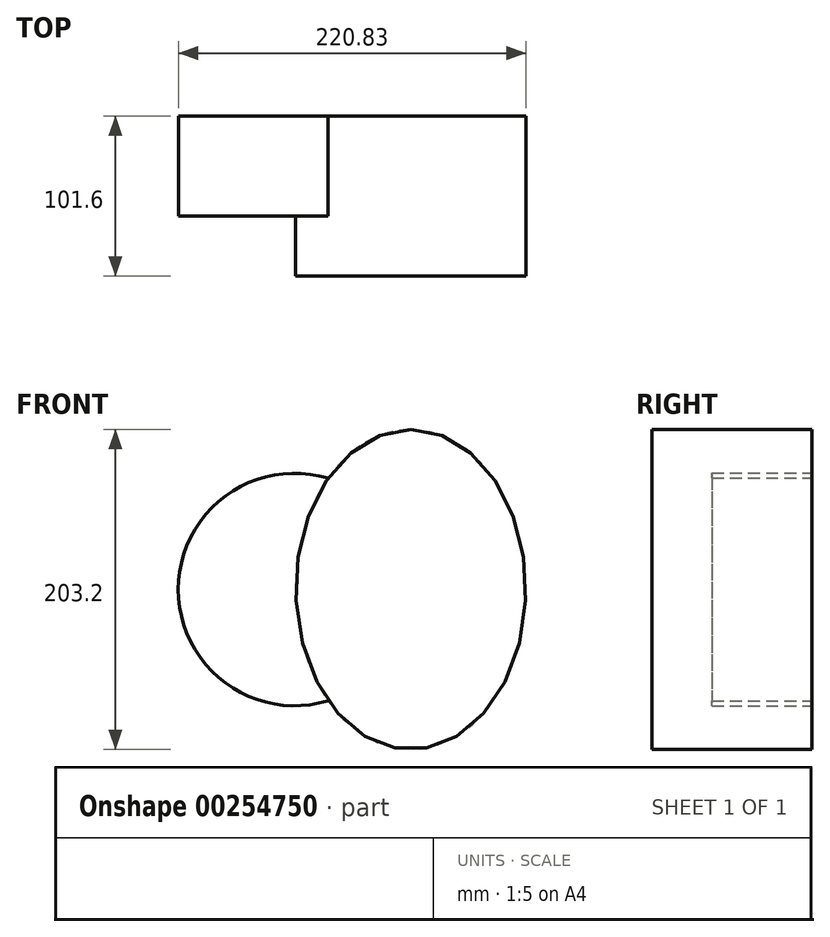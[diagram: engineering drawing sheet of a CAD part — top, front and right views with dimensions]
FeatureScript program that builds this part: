
annotation { "Feature Type Name" : "Feature", "Feature Type Description" : "" }
export const myFeature = defineFeature(function(context is Context, id is Id, definition is map)
    precondition{}
    {
        {
            var Q0;
            Q0=qCreatedBy(makeId("Front.planeOp"),FACE);
            var sketch = newSketch(context, id + "F0", { "sketchPlane" : qUnion([Q0])});
            skLineSegment(sketch, "E0", {"start": v(0, 0) * mm, "end": v(-76.2, 0) * mm});
            skCircle(sketch, "E1", {"center": v(-76.2, 0) * mm, "radius": 44.45 * mm});
            skLineSegment(sketch, "E2", {"start": v(-31.75, 0) * mm, "end": v(-31.75, -31.75) * mm});
            skCircle(sketch, "E3", {"center": v(0, 0) * mm, "radius": 73.85 * mm});
            skLineSegment(sketch, "E4", {"start": v(73.85, 0) * mm, "end": v(73.85, 101.6) * mm});
            skEllipse(sketch, "E5", {"center": v(73.85, 0) * mm, "majorRadius": 101.6 * mm, "minorRadius": 73.13 * mm, "majorAxis": v(0, 1)});
            skSolve(sketch);
        }
        {
            var Q0;
            {var subQ0=sQuery(id+"F0.wireOp",EDGE,"E3");var subQ1=sQuery(id+"F0.wireOp",EDGE,"E1");var subQ2=makeQuery(id+"F0.imprint","INTERSECT",VERTEX,{"disambiguationData":[OD(0.0)],"derivedFrom":[subQ1,subQ0]});Q0=makeQuery(id+"F0.imprint","IMPRINT",FACE,{"disambiguationData":[TD([[makeQuery(id+"F0.imprint","IMPRINT",EDGE,{"disambiguationData":[TD([[subQ2,-1.0]])],"derivedFrom":subQ1}),1.0]])]});}
            extrude(context, id + "F1", {"entities" : qUnion([Q0]), "depth" : 25.4 * mm});
        }
        {
            var Q0;
            {var subQ0=sQuery(id+"F0.wireOp",EDGE,"E1");var subQ1=sQuery(id+"F0.wireOp",EDGE,"E0");var subQ2=makeQuery(id+"F0.imprint","INTERSECT",VERTEX,{"derivedFrom":[subQ1,subQ0]});Q0=makeQuery(id+"F0.imprint","IMPRINT",FACE,{"disambiguationData":[TD([[makeQuery(id+"F0.imprint","IMPRINT",EDGE,{"disambiguationData":[TD([[subQ2,-1.0]])],"derivedFrom":subQ1}),-1.0]])]});}
            var Q1;
            {var subQ0=sQuery(id+"F0.wireOp",EDGE,"E1");var subQ1=sQuery(id+"F0.wireOp",EDGE,"E0");var subQ2=makeQuery(id+"F0.imprint","INTERSECT",VERTEX,{"derivedFrom":[subQ1,subQ0]});Q1=makeQuery(id+"F0.imprint","IMPRINT",FACE,{"disambiguationData":[TD([[makeQuery(id+"F0.imprint","IMPRINT",EDGE,{"disambiguationData":[TD([[subQ2,-1.0]])],"derivedFrom":subQ1}),1.0]])]});}
            var Q2;
            {var subQ1=sQuery(id+"F0.wireOp",EDGE,"E1");var subQ5=makeQuery(id+"F0.imprint","INTERSECT",VERTEX,{"derivedFrom":[sQuery(id+"F0.wireOp",EDGE,"E0"),subQ1]});Q2=makeQuery(id+"F0.imprint","IMPRINT",FACE,{"disambiguationData":[TD([[makeQuery(id+"F0.imprint","IMPRINT",EDGE,{"disambiguationData":[TD([[subQ5,-1.0]])],"derivedFrom":subQ1}),-1.0]])]});}
            extrude(context, id + "F2", {"entities" : qUnion([Q0, Q1, Q2]), "operationType" : NewBodyOperationType.ADD, "depth" : 63.5 * mm});
        }
        {
            var Q0;
            {var subQ0=sQuery(id+"F0.wireOp",EDGE,"E3");var subQ1=makeQuery(id+"F0.imprint","INTERSECT",VERTEX,{"derivedFrom":[subQ0,sQuery(id+"F0.wireOp",EDGE,"E4")]});Q0=makeQuery(id+"F0.imprint","IMPRINT",FACE,{"disambiguationData":[TD([[makeQuery(id+"F0.imprint","IMPRINT",EDGE,{"disambiguationData":[TD([[subQ1,-1.0]])],"derivedFrom":subQ0}),1.0]])]});}
            var Q1;
            {var subQ0=sQuery(id+"F0.wireOp",EDGE,"E4");Q1=makeQuery(id+"F0.imprint","IMPRINT",FACE,{"disambiguationData":[TD([[makeQuery(id+"F0.imprint","IMPRINT",EDGE,{"derivedFrom":subQ0}),1.0]])]});}
            var Q2;
            {var subQ0=sQuery(id+"F0.wireOp",EDGE,"E4");Q2=makeQuery(id+"F0.imprint","IMPRINT",FACE,{"disambiguationData":[TD([[makeQuery(id+"F0.imprint","IMPRINT",EDGE,{"derivedFrom":subQ0}),-1.0]])]});}
            extrude(context, id + "F3", {"entities" : qUnion([Q0, Q1, Q2]), "operationType" : NewBodyOperationType.ADD, "depth" : 101.6 * mm});
        }
    });
